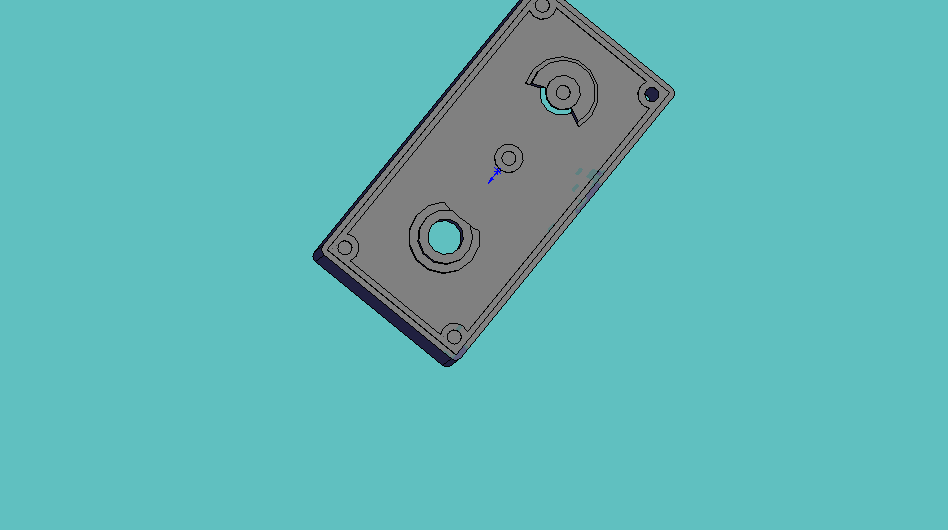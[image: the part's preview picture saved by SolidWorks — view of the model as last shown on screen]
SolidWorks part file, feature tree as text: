
SOLIDWORKS PART (.sldprt)
format: sldprt  version: not decoded by parser v0  size: 1,068,032 bytes
history: native  units: mm
features: sketch x18, extrude x11, cut_extrude x3, mirror x2, material x1, revolve x1, hole x1 (+14 scaffold rows collapsed)
feature tree (51):
  scaffold x14  (default folders/planes/origin — collapsed)
  material  "ABS"
  sketch  "Sketch1"  dims[c1.D3=4.699mm c1.D4=3.9624mm c1.D7=0.762mm c1.D1=19.685mm c1.D2=38.735mm c1.D5=20.574mm c1.D6=9.8425mm c2.D7=1.524mm c2.D8=1.524mm]
  extrude  "Extrude1"  Depth=1.190625mm
  sketch  "Sketch9"  dims[c1.D1=0.762mm c1.D2=1.5875mm c1.D3=3.81mm c1.D4=0.5842mm c1.D5=1.905mm c1.D6=1.27mm c2.D1=3.81mm c2.D3=3.302mm c2.D6=7.239mm c2.D7=8.255mm c2.D8=0.762mm c2.D9=5.3594mm]
  sketch  "Sketch6"  dims[D1=1.5875mm D2=3.175mm D3=11.3665mm]
  extrude  "Extrude3"  Depth=0.6096mm
  sketch  "Sketch7"  dims[D1=6.0mm]
  extrude  "Extrude4"  Depth=4.445mm
  sketch  "Sketch16"  dims[D1=7.874mm]
  extrude  "Extrude11"  Depth=1.905mm
  sketch  "Sketch17"  dims[D1=5.08mm]
  cut_extrude  "Cut-Extrude1"  [1 undecoded]
  sketch  "Sketch11"  dims[c1.D1=11.43mm c1.D2=~6.954201mm c2.D1=~10.610341mm c2.web width=1.143mm c2.D3=~1.044372mm c3.D1=14.605mm c3.D2=3.81mm c3.D3=1.905mm c3.D4=3.81mm c4.D1=1.27mm]
  extrude  "Extrude6"  Depth=4.572mm
  sketch  "Sketch10"  dims[c1.D1=0.0mm c1.D2=~1.190625mm c2.D1=0.0mm c2.D2=1.27mm]
  extrude  "Extrude5"  Depth=22.225mm
  sketch  "Sketch13"  dims[c1.D1=~10.753564mm c1.D2=12.7mm c2.D1=0.508mm c2.D5=1.143mm c2.D3=1.143mm c2.D2=1.905mm c2.D4=3.81mm c3.D5=1.27mm c3.D6=3.81mm c3.D7=1.27mm c3.D1=1.27mm c3.D8=14.605mm c4.D5=3.81mm c4.D6=14.605mm c5.D5=3.81mm c5.D6=14.605mm c6.D5=3.81mm]
  extrude  "Extrude8"  Depth=10.795mm
  sketch  "Sketch14"  dims[c1.D1=~0.396875mm c1.D2=1.5875mm c1.D3=~1.80975mm c2.D2=1.5875mm c2.D3=~0.396875mm c3.D2=1.5875mm c3.D3=1.016mm c3.D1=~1.619553mm c4.D1=45.0deg c4.D3=0.762mm c4.D4=2.032mm]
  extrude  "Extrude9"  Depth=0.762mm
  sketch  "Sketch23"
  cut_extrude  "Cut-Extrude2"  [1 undecoded]
  revolve  "Revolve1"  Angle=360deg
  sketch  "Sketch24"  dims[D1=7.62mm]
  cut_extrude  "Cut-Extrude3"  [1 undecoded]
  mirror  "Mirror1"
  mirror  "Mirror2"
  sketch  "Sketch18"  dims[D1=0.635mm]
  extrude  "Extrude12"  [1 undecoded]
  sketch  "Sketch19"  dims[D1=5.08mm D2=1.27mm D3=0.762mm D4=2.54mm]
  extrude  "Extrude13"  Depth=1.905mm
  sketch  "Sketch20"  dims[D1=3.81mm]
  extrude  "Extrude14"  Depth=1.016mm
  sketch  "Sketch21"
  hole  "#1-64 Tapped Hole1"  Diameter=1.5113mm Depth=5.588mm
  sketch  "3DSketch1"
  sketch  "Sketch22"  dims[hole-wizard template sketch: 28 standard entries collapsed; hole parameters kept: c8.Tap Drill Dia.=1.5113mm c8.Tap Drill Depth=5.588mm c8.Thread Major Dia.=1.8542mm c8.Thread Depth=3.7084mm c8.D5=~14.816244mm c8.Drill Angle=118.0deg c8.web width=1.143mm]
decode coverage: 27 of 36 modeling features carry decoded parameters
note: ~ marks probable driven/reference dimensions
note: 4 parameter values undecoded
summary: no parameter record found for 4 features
note: suppression state not decoded; provenance and decode notes live in map.json
